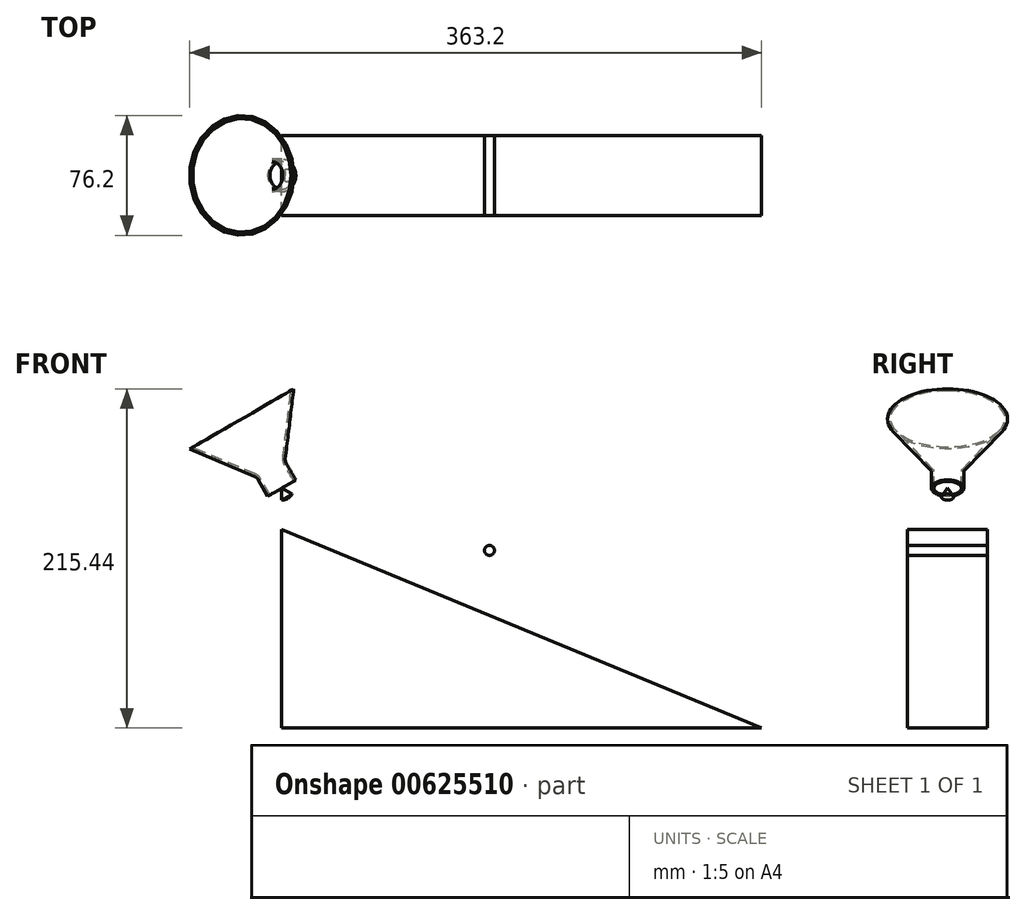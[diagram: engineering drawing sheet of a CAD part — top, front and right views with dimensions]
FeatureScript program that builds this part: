
annotation { "Feature Type Name" : "Feature", "Feature Type Description" : "" }
export const myFeature = defineFeature(function(context is Context, id is Id, definition is map)
    precondition{}
    {
        {
            var Q0;
            Q0=qCreatedBy(makeId("Front.planeOp"),FACE);
            var sketch = newSketch(context, id + "F0", { "sketchPlane" : qUnion([Q0])});
            skLineSegment(sketch, "E0", {"start": v(0, 0) * mm, "end": v(-304.8, 0) * mm});
            skLineSegment(sketch, "E1", {"start": v(-363.2, 177.34) * mm, "end": v(-320.6, 159.15) * mm});
            skLineSegment(sketch, "E2", {"start": v(-304.8, 152.4) * mm, "end": v(-304.8, 0) * mm});
            skLineSegment(sketch, "E3", {"start": v(-330.2, 196.4) * mm, "end": v(-304.8, 152.4) * mm, "construction": true});
            skLineSegment(sketch, "E4", {"start": v(-363.2, 177.34) * mm, "end": v(-361.46, 178.34) * mm});
            skPoint(sketch, "E5.start.orphan", {"position": v(-363.2, 253.54) * mm});
            skLineSegment(sketch, "E6", {"start": v(-320.6, 159.15) * mm, "end": v(-313.73, 147.24) * mm});
            skLineSegment(sketch, "E7", {"start": v(-313.73, 147.24) * mm, "end": v(-312.34, 148.04) * mm});
            skLineSegment(sketch, "E8.MirrorCS", {"start": v(-302.74, 169.46) * mm, "end": v(-295.87, 157.56) * mm});
            skCircle(sketch, "E9", {"center": v(-304.8, 152.4) * mm, "radius": 7.62 * mm});
            skLineSegment(sketch, "E10.MirrorCS", {"start": v(-297.2, 215.44) * mm, "end": v(-302.74, 169.46) * mm});
            skLineSegment(sketch, "E11", {"start": v(-361.46, 178.34) * mm, "end": v(-319.49, 160.41) * mm});
            skLineSegment(sketch, "E12", {"start": v(-319.49, 160.41) * mm, "end": v(-312.34, 148.04) * mm});
            skLineSegment(sketch, "E13", {"start": v(-361.46, 178.34) * mm, "end": v(-330.2, 196.4) * mm, "construction": true});
            skLineSegment(sketch, "E14", {"start": v(-312.34, 148.04) * mm, "end": v(-304.8, 152.4) * mm, "construction": true});
            skLineSegment(sketch, "E15", {"start": v(-308.6, 159) * mm, "end": v(-300.99, 145.8) * mm});
            skPoint(sketch, "E16.orphan", {"position": v(-304.8, 56.75) * mm});
            skLineSegment(sketch, "E17", {"start": v(-304.8, 126.25) * mm, "end": v(0, 0) * mm});
            skCircle(sketch, "E18", {"center": v(-231.48, 104.13) * mm, "radius": 7.62 * mm});
            skLineSegment(sketch, "E19", {"start": v(-304.8, 126.25) * mm, "end": v(-300.9, 135.68) * mm});
            skCircle(sketch, "E20", {"center": v(-172.89, 112.85) * mm, "radius": 38.1 * mm});
            skLineSegment(sketch, "E21", {"start": v(-172.89, 112.85) * mm, "end": v(-187.47, 77.65) * mm, "construction": true});
            skCircle(sketch, "E22", {"center": v(-172.89, 112.85) * mm, "radius": 3.18 * mm});
            skCircle(sketch, "E23", {"center": v(-172.89, 112.85) * mm, "radius": 31.75 * mm});
            skLineSegment(sketch, "E24", {"start": v(-192.56, 87.93) * mm, "end": v(-176.6, 103.9) * mm});
            skLineSegment(sketch, "E25", {"start": v(-176.6, 103.9) * mm, "end": v(-176.6, 81.32) * mm});
            skLineSegment(sketch, "E26.1.0", {"start": v(-1.68, -204.89) * mm, "end": v(17.87, -193.6) * mm});
            skPoint(sketch, "E26.center", {"position": v(0, 0) * mm});
            skCircle(sketch, "E27", {"center": v(-187.72, 123.36) * mm, "radius": 3.05 * mm});
            skCircle(sketch, "E28.1.0", {"center": v(-12.97, -224.25) * mm, "radius": 3.05 * mm});
            skCircle(sketch, "E28.2.0", {"center": v(200.7, 100.9) * mm, "radius": 3.05 * mm});
            skLineSegment(sketch, "E29.bottom", {"start": v(-169.71, 116.03) * mm, "end": v(-176.06, 116.03) * mm});
            skLineSegment(sketch, "E29.top", {"start": v(-169.71, 109.68) * mm, "end": v(-176.06, 109.68) * mm});
            skLineSegment(sketch, "E29.left", {"start": v(-169.71, 116.03) * mm, "end": v(-169.71, 109.68) * mm});
            skLineSegment(sketch, "E29.right", {"start": v(-176.06, 116.03) * mm, "end": v(-176.06, 109.68) * mm});
            skSolve(sketch);
        }
        {
            var Q0;
            Q0=makeQuery(id+"F0.imprint","IMPRINT",FACE,{"disambiguationData":[TD([[makeQuery(id+"F0.imprint","IMPRINT",EDGE,{"derivedFrom":sQuery(id+"F0.wireOp",EDGE,"E1")}),1.0]])]});
            var Q1;
            Q1=sQuery(id+"F0.wireOp",EDGE,"E3");
            revolve(context, id + "F1", {"entities" : qUnion([Q0]), "axis" : qUnion([Q1]), "revolveType" : RevolveType.FULL});
        }
        {
            var Q0;
            {var subQ0=sQuery(id+"F0.wireOp",EDGE,"E15");var subQ1=sQuery(id+"F0.wireOp",EDGE,"E9");var subQ2=makeQuery(id+"F0.imprint","INTERSECT",VERTEX,{"disambiguationData":[OD(0.0)],"derivedFrom":[subQ1,subQ0]});Q0=makeQuery(id+"F0.imprint","IMPRINT",FACE,{"disambiguationData":[TD([[makeQuery(id+"F0.imprint","IMPRINT",EDGE,{"disambiguationData":[TD([[subQ2,1.0]])],"derivedFrom":subQ1}),1.0]])]});}
            var Q1;
            Q1=sQuery(id+"F0.wireOp",EDGE,"E15");
            revolve(context, id + "F2", {"entities" : qUnion([Q0]), "axis" : qUnion([Q1]), "revolveType" : RevolveType.FULL});
        }
        {
            var Q0;
            Q0=makeQuery(id+"F1.opRevolve","SWEPT_EDGE",EDGE,{"disambiguationData":[OSD([sQuery(id+"F0.wireOp",EDGE,"E11"),sQuery(id+"F0.wireOp",EDGE,"E12")])]});
            fillet(context, id + "F3", {"entities" : qUnion([Q0]), "radius" : 6.35 * mm, "tangentPropagation" : true, "allowEdgeOverflow" : false});
        }
        {
            var Q0;
            Q0=makeQuery(id+"F1.opRevolve","SWEPT_EDGE",EDGE,{"disambiguationData":[OSD([sQuery(id+"F0.wireOp",EDGE,"E1"),sQuery(id+"F0.wireOp",EDGE,"E6")])]});
            fillet(context, id + "F4", {"entities" : qUnion([Q0]), "radius" : 4.78 * mm, "tangentPropagation" : true, "allowEdgeOverflow" : false});
        }
        {
            var Q0;
            {var subQ0=sQuery(id+"F0.wireOp",EDGE,"E22");var subQ1=makeQuery(id+"F0.imprint","INTERSECT",VERTEX,{"derivedFrom":[subQ0,sQuery(id+"F0.wireOp",EDGE,"E29.bottom")]});Q0=makeQuery(id+"F0.imprint","IMPRINT",FACE,{"disambiguationData":[TD([[makeQuery(id+"F0.imprint","IMPRINT",EDGE,{"disambiguationData":[TD([[subQ1,1.0]])],"derivedFrom":subQ0}),1.0]])]});}
            var Q1;
            {var subQ4=sQuery(id+"F0.wireOp",EDGE,"E0");Q1=makeQuery(id+"F0.imprint","IMPRINT",FACE,{"disambiguationData":[TD([[makeQuery(id+"F0.imprint","IMPRINT",EDGE,{"derivedFrom":subQ4}),-1.0]])]});}
            extrude(context, id + "F5", {"entities" : qUnion([Q0, Q1]), "endBound" : BoundingType.SYMMETRIC, "depth" : 50.8 * mm, "offsetDistance" : 25.4 * mm});
        }
    });
